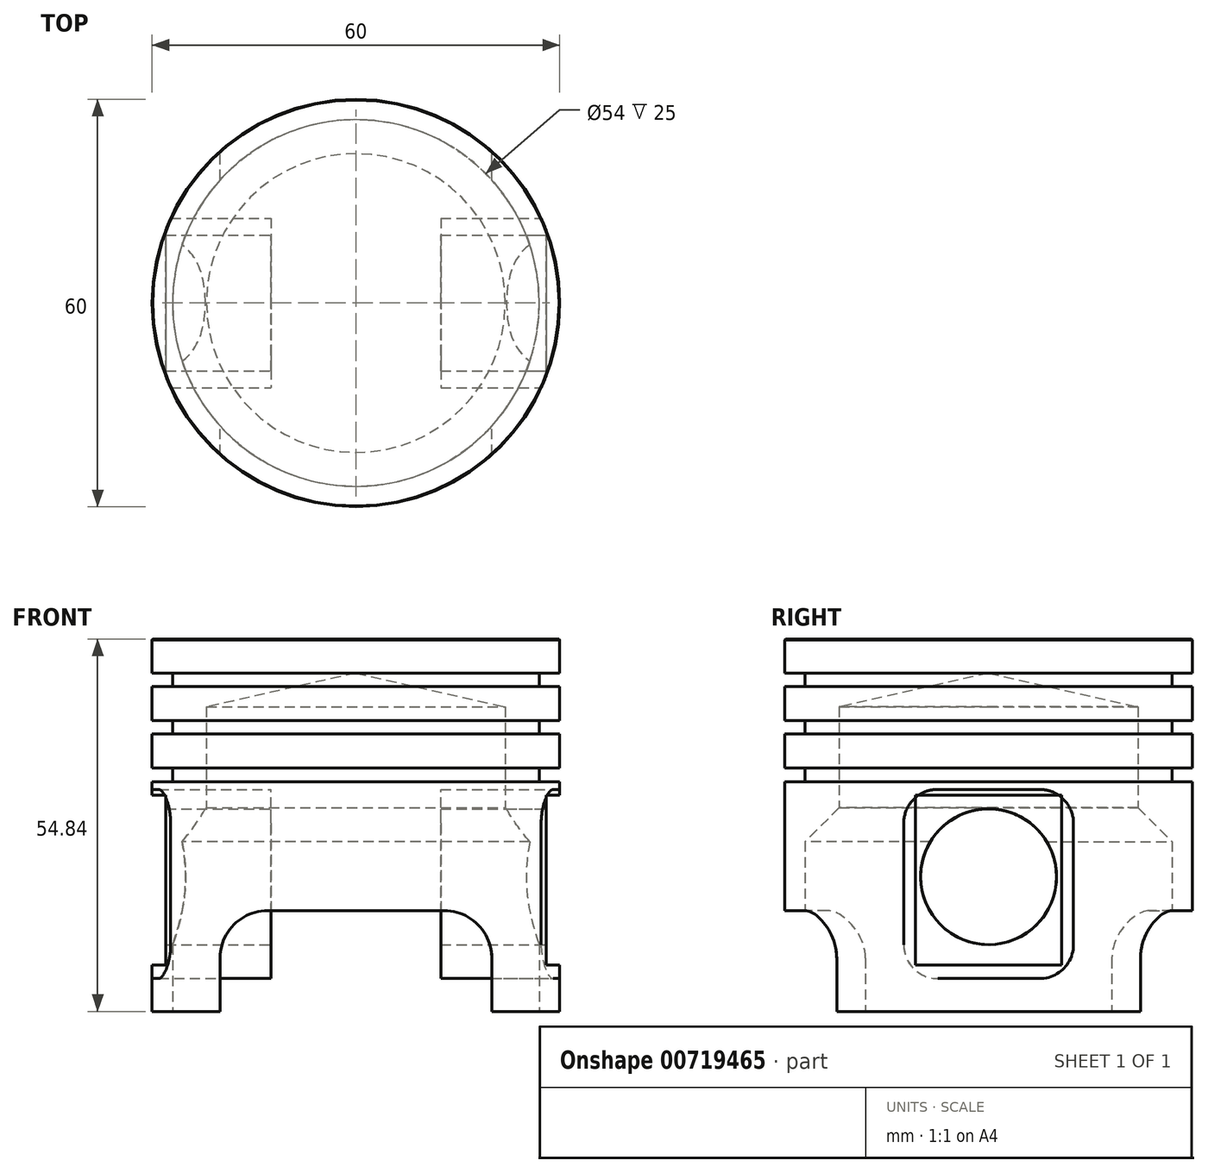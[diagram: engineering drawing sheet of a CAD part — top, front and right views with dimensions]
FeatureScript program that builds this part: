
annotation { "Feature Type Name" : "Feature", "Feature Type Description" : "" }
export const myFeature = defineFeature(function(context is Context, id is Id, definition is map)
    precondition{}
    {
        {
            var Q0;
            Q0=qCreatedBy(makeId("Front.planeOp"),FACE);
            var sketch = newSketch(context, id + "F0", { "sketchPlane" : qUnion([Q0])});
            skLineSegment(sketch, "E0.bottom", {"start": v(27, 0.16) * mm, "end": v(30, 0.16) * mm});
            skLineSegment(sketch, "E0.top", {"start": v(0, 55) * mm, "end": v(30, 55) * mm});
            skLineSegment(sketch, "E0.left", {"start": v(0, 50) * mm, "end": v(0, 55) * mm});
            skLineSegment(sketch, "E0.right", {"start": v(30, 0.16) * mm, "end": v(30, 34) * mm});
            skLineSegment(sketch, "E1.bottom", {"start": v(27, 50) * mm, "end": v(30, 50) * mm});
            skLineSegment(sketch, "E1.top", {"start": v(27, 48) * mm, "end": v(30, 48) * mm});
            skLineSegment(sketch, "E1.left", {"start": v(27, 50) * mm, "end": v(27, 48) * mm});
            skLineSegment(sketch, "E2.bottom", {"start": v(27, 43) * mm, "end": v(30, 43) * mm});
            skLineSegment(sketch, "E2.top", {"start": v(27, 41) * mm, "end": v(30, 41) * mm});
            skLineSegment(sketch, "E2.left", {"start": v(27, 43) * mm, "end": v(27, 41) * mm});
            skLineSegment(sketch, "E3.bottom", {"start": v(27, 36) * mm, "end": v(30, 36) * mm});
            skLineSegment(sketch, "E3.top", {"start": v(27, 34) * mm, "end": v(30, 34) * mm});
            skLineSegment(sketch, "E3.left", {"start": v(27, 36) * mm, "end": v(27, 34) * mm});
            skLineSegment(sketch, "E4.trimOffspring", {"start": v(30, 50) * mm, "end": v(30, 55) * mm});
            skLineSegment(sketch, "E5.trimOffspring", {"start": v(30, 43) * mm, "end": v(30, 48) * mm});
            skLineSegment(sketch, "E6.trimOffspring", {"start": v(30, 36) * mm, "end": v(30, 41) * mm});
            skLineSegment(sketch, "E7", {"start": v(27, 0.16) * mm, "end": v(27, 25.16) * mm});
            skLineSegment(sketch, "E8", {"start": v(27, 25.16) * mm, "end": v(22, 30.16) * mm});
            skLineSegment(sketch, "E9", {"start": v(22, 30.16) * mm, "end": v(22, 45) * mm});
            skLineSegment(sketch, "E10", {"start": v(22, 45) * mm, "end": v(0, 50) * mm});
            skSolve(sketch);
        }
        {
            var Q0;
            Q0=makeQuery(id+"F0.imprint","IMPRINT",FACE,{"disambiguationData":[TD([[makeQuery(id+"F0.imprint","IMPRINT",EDGE,{"derivedFrom":sQuery(id+"F0.wireOp",EDGE,"E0.bottom")}),1.0]])]});
            var Q1;
            Q1=sQuery(id+"F0.wireOp",EDGE,"E0.left");
            revolve(context, id + "F1", {"surfaceOperationType" : NewSurfaceOperationType.NEW, "entities" : qUnion([Q0]), "axis" : qUnion([Q1]), "revolveType" : RevolveType.FULL});
        }
        {
            var Q0;
            Q0=qCreatedBy(makeId("Front.planeOp"),FACE);
            var sketch = newSketch(context, id + "F2", { "sketchPlane" : qUnion([Q0])});
            skLineSegment(sketch, "E11.bottom", {"start": v(13, 15) * mm, "end": v(-13, 15) * mm});
            skLineSegment(sketch, "E11.top", {"start": v(20, -15) * mm, "end": v(-20, -15) * mm});
            skLineSegment(sketch, "E11.left", {"start": v(20, 8) * mm, "end": v(20, -15) * mm});
            skLineSegment(sketch, "E11.right", {"start": v(-20, 8) * mm, "end": v(-20, -15) * mm});
            skPoint(sketch, "E11.middle", {"position": v(0, 0) * mm});
            skPoint(sketch, "E12.visualSharp", {"position": v(-20, 15) * mm});
            skArc(sketch, "E12.filletArc", {"start": v(-13, 15) * mm, "mid": v(-17.95, 12.95) * mm, "end": v(-20, 8) * mm});
            skPoint(sketch, "E13.visualSharp", {"position": v(20, 15) * mm});
            skArc(sketch, "E13.filletArc", {"start": v(20, 8) * mm, "mid": v(17.95, 12.95) * mm, "end": v(13, 15) * mm});
            skSolve(sketch);
        }
        {
            var Q0;
            Q0=makeQuery(id+"F2.imprint","IMPRINT",FACE,{"disambiguationData":[TD([[makeQuery(id+"F2.imprint","IMPRINT",EDGE,{"derivedFrom":sQuery(id+"F2.wireOp",EDGE,"E11.bottom")}),1.0]])]});
            extrude(context, id + "F3", {"entities" : qUnion([Q0]), "operationType" : NewBodyOperationType.REMOVE, "oppositeDirection" : true, "depth" : 100 * mm, "offsetDistance" : 25 * mm, "symmetric" : true});
        }
        {
            var Q0;
            Q0=qCreatedBy(makeId("Top.planeOp"),FACE);
            cPlane(context, id + "F4", {"entities" : qUnion([Q0]), "cplaneType" : CPlaneType.OFFSET, "offset" : 5 * mm, "width" : 150 * mm, "height" : 150 * mm});
        }
        {
            var Q0;
            Q0=qCreatedBy(id+"F4.planeOp",FACE);
            var sketch = newSketch(context, id + "F5", { "sketchPlane" : qUnion([Q0])});
            skArc(sketch, "E14.0", {"start": v(-27.27, 12.5) * mm, "mid": v(-30, 0) * mm, "end": v(-27.27, -12.5) * mm});
            skLineSegment(sketch, "E15.bottom", {"start": v(-27.27, -12.5) * mm, "end": v(-12.5, -12.5) * mm});
            skLineSegment(sketch, "E15.top", {"start": v(-27.27, 12.5) * mm, "end": v(-12.5, 12.5) * mm});
            skLineSegment(sketch, "E16.left", {"start": v(12.5, 12.5) * mm, "end": v(12.5, -12.5) * mm});
            skLineSegment(sketch, "E16.right", {"start": v(-12.5, 12.5) * mm, "end": v(-12.5, -12.5) * mm});
            skPoint(sketch, "E15.left.end.orphan", {"position": v(-44.06, 12.5) * mm});
            skPoint(sketch, "E17.orphan", {"position": v(-42.81, -12.5) * mm});
            skPoint(sketch, "E15.right.end.orphan", {"position": v(42.81, 12.5) * mm});
            skPoint(sketch, "E18.orphan", {"position": v(44.06, -12.5) * mm});
            skLineSegment(sketch, "E19.trimOffspring", {"start": v(12.5, -12.5) * mm, "end": v(27.27, -12.5) * mm});
            skLineSegment(sketch, "E20.trimOffspring", {"start": v(12.5, 12.5) * mm, "end": v(27.27, 12.5) * mm});
            skCircle(sketch, "E21", {"center": v(0, 0) * mm, "radius": 30 * mm});
            skArc(sketch, "E22.trimOffspring", {"start": v(27.27, -12.5) * mm, "mid": v(30, 0) * mm, "end": v(27.27, 12.5) * mm});
            skSolve(sketch);
        }
        {
            var Q0;
            Q0=makeQuery(id+"F5.imprint","IMPRINT",FACE,{"disambiguationData":[TD([[makeQuery(id+"F5.imprint","IMPRINT",EDGE,{"derivedFrom":sQuery(id+"F5.wireOp",EDGE,"E16.left")}),1.0]])]});
            var Q1;
            {var subQ0=sQuery(id+"F5.wireOp",EDGE,"E15.bottom");Q1=makeQuery(id+"F5.imprint","IMPRINT",FACE,{"disambiguationData":[TD([[makeQuery(id+"F5.imprint","IMPRINT",EDGE,{"derivedFrom":subQ0}),1.0]])]});}
            extrude(context, id + "F6", {"entities" : qUnion([Q0, Q1]), "depth" : 27.87 * mm, "offsetDistance" : 25 * mm});
        }
        {
            var Q0;
            Q0=makeQuery(id+"F6.opExtrude","CAP_EDGE",EDGE,{"disambiguationData":[OSD([sQuery(id+"F5.wireOp",EDGE,"E19.trimOffspring")])],"isStart":true});
            var Q1;
            Q1=makeQuery(id+"F6.opExtrude","CAP_EDGE",EDGE,{"disambiguationData":[OSD([sQuery(id+"F5.wireOp",EDGE,"E20.trimOffspring")])],"isStart":true});
            var Q2;
            Q2=makeQuery(id+"F6.opExtrude","CAP_EDGE",EDGE,{"disambiguationData":[OSD([sQuery(id+"F5.wireOp",EDGE,"E15.top")])],"isStart":true});
            var Q3;
            Q3=makeQuery(id+"F6.opExtrude","CAP_EDGE",EDGE,{"disambiguationData":[OSD([sQuery(id+"F5.wireOp",EDGE,"E15.bottom")])],"isStart":true});
            var Q4;
            Q4=makeQuery(id+"F6.opExtrude","CAP_EDGE",EDGE,{"disambiguationData":[OSD([sQuery(id+"F5.wireOp",EDGE,"E15.bottom")])],"isStart":false});
            var Q5;
            Q5=makeQuery(id+"F6.opExtrude","CAP_EDGE",EDGE,{"disambiguationData":[OSD([sQuery(id+"F5.wireOp",EDGE,"E19.trimOffspring")])],"isStart":false});
            var Q6;
            Q6=makeQuery(id+"F6.opExtrude","CAP_EDGE",EDGE,{"disambiguationData":[OSD([sQuery(id+"F5.wireOp",EDGE,"E15.top")])],"isStart":false});
            var Q7;
            Q7=makeQuery(id+"F6.opExtrude","CAP_EDGE",EDGE,{"disambiguationData":[OSD([sQuery(id+"F5.wireOp",EDGE,"E20.trimOffspring")])],"isStart":false});
            fillet(context, id + "F7", {"entities" : qUnion([Q0, Q1, Q2, Q3, Q4, Q5, Q6, Q7]), "radius" : 5 * mm, "tangentPropagation" : true, "allowEdgeOverflow" : false});
        }
        {
            var Q0;
            Q0=qCreatedBy(makeId("Right.planeOp"),FACE);
            var sketch = newSketch(context, id + "F8", { "sketchPlane" : qUnion([Q0])});
            skCircle(sketch, "E23", {"center": v(0, 20) * mm, "radius": 10 * mm});
            skSolve(sketch);
        }
        {
            var Q0;
            Q0=makeQuery(id+"F8.imprint","IMPRINT",FACE,{"disambiguationData":[TD([[makeQuery(id+"F8.imprint","IMPRINT",EDGE,{"derivedFrom":sQuery(id+"F8.wireOp",EDGE,"E23")}),1.0]])]});
            extrude(context, id + "F9", {"entities" : qUnion([Q0]), "operationType" : NewBodyOperationType.REMOVE, "oppositeDirection" : true, "depth" : 100 * mm, "offsetDistance" : 25 * mm, "symmetric" : true});
        }
        {
            var Q0;
            Q0=qCreatedBy(makeId("Front.planeOp"),FACE);
            var sketch = newSketch(context, id + "F10", { "sketchPlane" : qUnion([Q0])});
            skLineSegment(sketch, "E24.bottom", {"start": v(28, 32) * mm, "end": v(33, 32) * mm});
            skLineSegment(sketch, "E24.top", {"start": v(28, 7) * mm, "end": v(33, 7) * mm});
            skLineSegment(sketch, "E24.left", {"start": v(28, 32) * mm, "end": v(28, 7) * mm});
            skLineSegment(sketch, "E24.right", {"start": v(33, 32) * mm, "end": v(33, 7) * mm});
            skLineSegment(sketch, "E25", {"start": v(0, 0) * mm, "end": v(0, 61.7) * mm, "construction": true});
            skLineSegment(sketch, "E26.MirrorCS", {"start": v(-33, 32) * mm, "end": v(-33, 7) * mm});
            skLineSegment(sketch, "E27.MirrorCS", {"start": v(-28, 32) * mm, "end": v(-28, 7) * mm});
            skLineSegment(sketch, "E28.MirrorCS", {"start": v(-28, 32) * mm, "end": v(-33, 32) * mm});
            skLineSegment(sketch, "E29.MirrorCS", {"start": v(-28, 7) * mm, "end": v(-33, 7) * mm});
            skSolve(sketch);
        }
        {
            var Q0;
            Q0=makeQuery(id+"F10.imprint","IMPRINT",FACE,{"disambiguationData":[TD([[makeQuery(id+"F10.imprint","IMPRINT",EDGE,{"derivedFrom":sQuery(id+"F10.wireOp",EDGE,"E26.MirrorCS")}),1.0]])]});
            var Q1;
            Q1=makeQuery(id+"F10.imprint","IMPRINT",FACE,{"disambiguationData":[TD([[makeQuery(id+"F10.imprint","IMPRINT",EDGE,{"derivedFrom":sQuery(id+"F10.wireOp",EDGE,"E24.bottom")}),-1.0]])]});
            extrude(context, id + "F11", {"entities" : qUnion([Q0, Q1]), "operationType" : NewBodyOperationType.REMOVE, "oppositeDirection" : true, "depth" : 25 * mm, "offsetDistance" : 25 * mm, "symmetric" : true});
        }
        {
            var Q0;
            Q0=makeQuery(id+"F1.opRevolve","SWEPT_EDGE",EDGE,{"disambiguationData":[OSD([sQuery(id+"F0.wireOp",EDGE,"E0.top"),sQuery(id+"F0.wireOp",EDGE,"E4.trimOffspring")])]});
            chamfer(context, id + "F12", {"entities" : qUnion([Q0]), "width" : 0.1 * mm, "tangentPropagation" : true});
        }
    });
